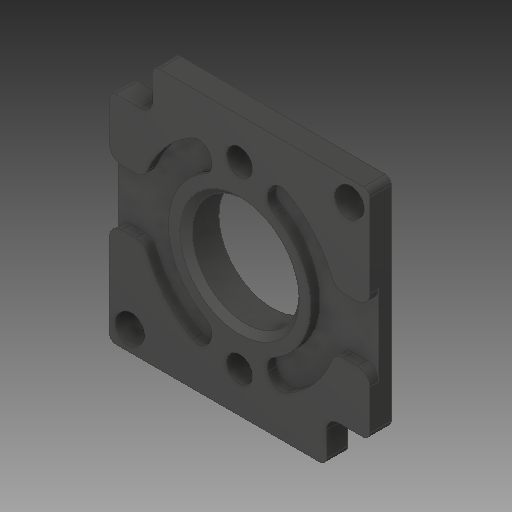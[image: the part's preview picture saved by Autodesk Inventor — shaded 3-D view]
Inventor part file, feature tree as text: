
AUTODESK INVENTOR PART (.ipt)
format: ipt  version: 2017 (Build 210142000, 142)  size: 277,504 bytes
history: native  units: in
note: dims shown in document units (in); Inventor stores cm internally (conversion verified against a paired STEP export)
features: fillet x1
ambient origin geometry x8: Origin, YZ Plane, XZ Plane, XY Plane, X Axis, Y Axis, Z Axis, Center Point
bodies: Solid1 (feature_tree)
feature tree (1):
  fillet  "Fillet4"  [1 undecoded]
note: 1 required parameter value undecoded (feature->parameter linkage not recoverable at this tier; creation-order binding heuristic only, values carry confidence <= 0.55)
